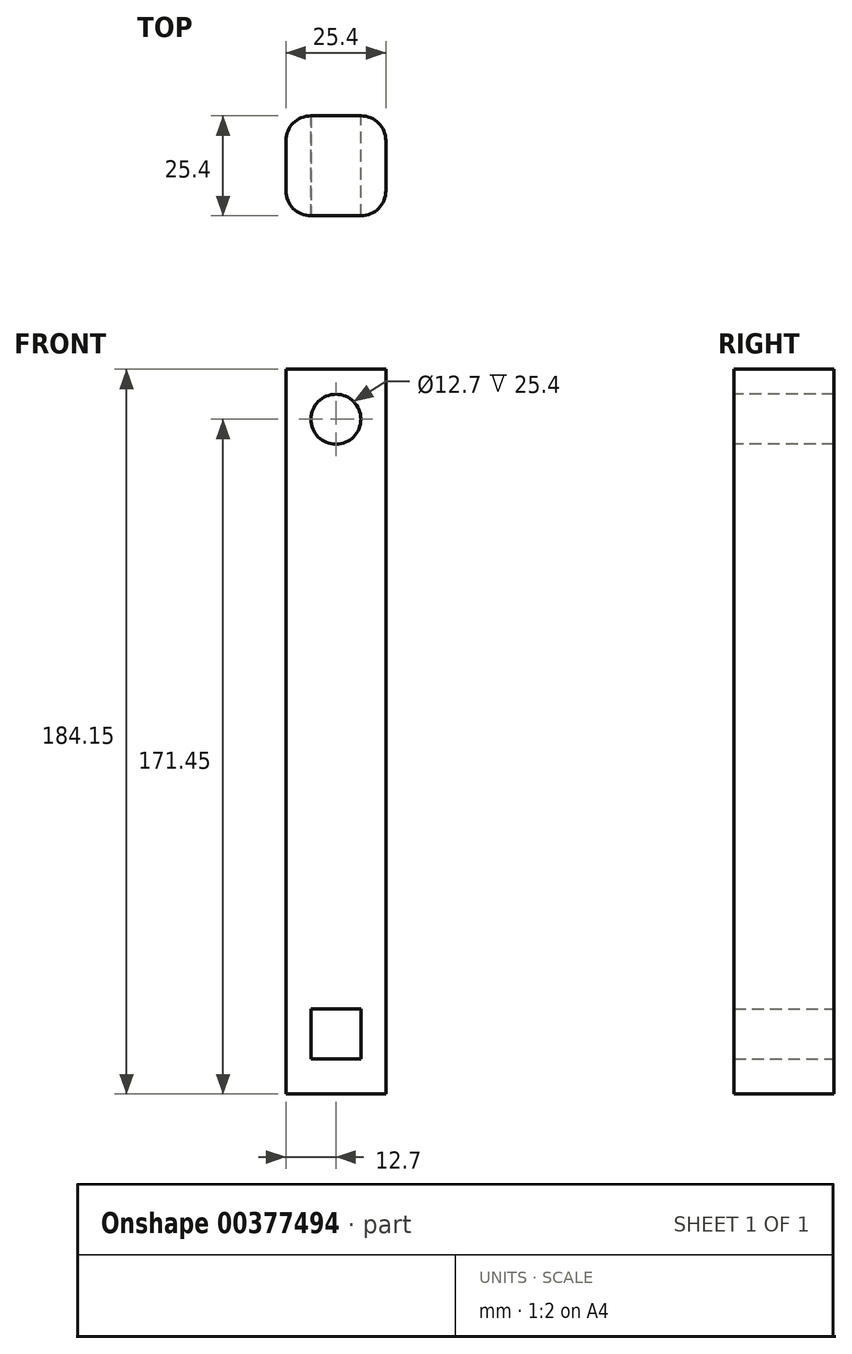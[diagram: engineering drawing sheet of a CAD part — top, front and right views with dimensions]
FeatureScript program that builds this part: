
annotation { "Feature Type Name" : "Feature", "Feature Type Description" : "" }
export const myFeature = defineFeature(function(context is Context, id is Id, definition is map)
    precondition{}
    {
        {
            var Q0;
            Q0=qCreatedBy(makeId("Front.planeOp"),FACE);
            var sketch = newSketch(context, id + "F0", { "sketchPlane" : qUnion([Q0])});
            skLineSegment(sketch, "E0", {"start": v(0, -32) * mm, "end": v(-12.7, -32) * mm});
            skLineSegment(sketch, "E1", {"start": v(-12.7, -32) * mm, "end": v(-12.7, 69.6) * mm});
            skLineSegment(sketch, "E2.MirrorCS", {"start": v(0, -32) * mm, "end": v(12.7, -32) * mm});
            skLineSegment(sketch, "E3.MirrorCS", {"start": v(12.7, -32) * mm, "end": v(12.7, 69.6) * mm});
            skLineSegment(sketch, "E4", {"start": v(12.7, 69.6) * mm, "end": v(-12.7, 69.6) * mm});
            skSolve(sketch);
        }
        {
            var Q0;
            Q0=qSketchRegion(id+"F0",true);
            extrude(context, id + "F1", {"entities" : qUnion([Q0]), "depth" : 25.4 * mm});
        }
        {
            var Q0;
            Q0=makeQuery(id+"F1.opExtrude","CAP_FACE",FACE,{"disambiguationData":[OSD([sQuery(id+"F0.wireOp",EDGE,"E0"),sQuery(id+"F0.wireOp",EDGE,"E1"),sQuery(id+"F0.wireOp",EDGE,"E2.MirrorCS"),sQuery(id+"F0.wireOp",EDGE,"E3.MirrorCS"),sQuery(id+"F0.wireOp",EDGE,"E4")])],"isStart":false});
            var sketch = newSketch(context, id + "F2", { "sketchPlane" : qUnion([Q0])});
            skLineSegment(sketch, "E5", {"start": v(0, 69.6) * mm, "end": v(0, -32) * mm});
            skLineSegment(sketch, "E6", {"start": v(0, -32) * mm, "end": v(0, 18.8) * mm});
            skLineSegment(sketch, "E7", {"start": v(0, 18.8) * mm, "end": v(0, -6.6) * mm});
            skLineSegment(sketch, "E8", {"start": v(0, -6.6) * mm, "end": v(0, 18.8) * mm});
            skLineSegment(sketch, "E9", {"start": v(0, 18.8) * mm, "end": v(0, 69.6) * mm});
            skLineSegment(sketch, "E10", {"start": v(0, 69.6) * mm, "end": v(0, 44.2) * mm});
            skLineSegment(sketch, "E11", {"start": v(0, 69.6) * mm, "end": v(0, 56.9) * mm});
            skLineSegment(sketch, "E12", {"start": v(0, -32) * mm, "end": v(0, -6.6) * mm});
            skLineSegment(sketch, "E13", {"start": v(0, -6.6) * mm, "end": v(0, -19.3) * mm});
            skSolve(sketch);
        }
        {
            var Q0;
            Q0=sQuery(id+"F2.wireOp",VERTEX,"E11.end");
            var Q1;
            Q1=makeQuery(id+"F1.opExtrude","SWEPT_BODY",BODY,{"disambiguationData":[OSD([sQuery(id+"F0.wireOp",EDGE,"E0"),sQuery(id+"F0.wireOp",EDGE,"E1"),sQuery(id+"F0.wireOp",EDGE,"E2.MirrorCS"),sQuery(id+"F0.wireOp",EDGE,"E3.MirrorCS"),sQuery(id+"F0.wireOp",EDGE,"E4")])]});
            hole(context, id + "F3", {"style" : HoleStyle.SIMPLE, "endStyle" : HoleEndStyle.BLIND, "holeDiameter" : 12.7 * mm, "holeDepth" : 254 * mm, "tappedDepth" : 12.7 * mm, "tapClearance" : 3, "locations" : qUnion([Q0]), "scope" : qUnion([Q1])});
        }
        {
            var Q0;
            Q0=makeQuery(id+"F1.opExtrude","CAP_FACE",FACE,{"disambiguationData":[OSD([sQuery(id+"F0.wireOp",EDGE,"E0"),sQuery(id+"F0.wireOp",EDGE,"E1"),sQuery(id+"F0.wireOp",EDGE,"E2.MirrorCS"),sQuery(id+"F0.wireOp",EDGE,"E3.MirrorCS"),sQuery(id+"F0.wireOp",EDGE,"E4")])],"isStart":false});
            var sketch = newSketch(context, id + "F4", { "sketchPlane" : qUnion([Q0])});
            skLineSegment(sketch, "E14", {"start": v(12.7, -32) * mm, "end": v(12.7, -114.56) * mm});
            skLineSegment(sketch, "E15", {"start": v(-12.7, -32) * mm, "end": v(-12.7, -114.56) * mm});
            skLineSegment(sketch, "E16", {"start": v(12.7, -114.56) * mm, "end": v(-12.7, -114.56) * mm});
            skSolve(sketch);
        }
        {
            var Q0;
            Q0=makeQuery(id+"F4.imprint","IMPRINT",FACE,{"disambiguationData":[TD([[makeQuery(id+"F4.imprint","IMPRINT",EDGE,{"derivedFrom":sQuery(id+"F4.wireOp",EDGE,"E14")}),-1.0]])]});
            extrude(context, id + "F5", {"entities" : qUnion([Q0]), "operationType" : NewBodyOperationType.ADD, "depth" : -25.4 * mm});
        }
        {
            var Q0;
            {var subQ0=sQuery(id+"F0.wireOp",EDGE,"E2.MirrorCS");var subQ1=sQuery(id+"F0.wireOp",EDGE,"E0");Q0=makeQuery(id+"F5.boolean.opBoolean","MERGE",FACE,{"derivedFrom":[makeQuery(id+"F1.opExtrude","CAP_FACE",FACE,{"disambiguationData":[OSD([subQ1,sQuery(id+"F0.wireOp",EDGE,"E1"),subQ0,sQuery(id+"F0.wireOp",EDGE,"E3.MirrorCS"),sQuery(id+"F0.wireOp",EDGE,"E4")])],"isStart":true}),makeQuery(id+"F5.opExtrude","CAP_FACE",FACE,{"disambiguationData":[OSD([subQ1,subQ0,sQuery(id+"F4.wireOp",EDGE,"E14"),sQuery(id+"F4.wireOp",EDGE,"E15"),sQuery(id+"F4.wireOp",EDGE,"E16")])],"isStart":false})]});}
            var sketch = newSketch(context, id + "F6", { "sketchPlane" : qUnion([Q0])});
            skLineSegment(sketch, "E17", {"start": v(0, -114.56) * mm, "end": v(0, -99.32) * mm});
            skLineSegment(sketch, "E18.bottom", {"start": v(6.35, -105.67) * mm, "end": v(-6.35, -105.67) * mm});
            skLineSegment(sketch, "E18.top", {"start": v(6.35, -92.97) * mm, "end": v(-6.35, -92.97) * mm});
            skLineSegment(sketch, "E18.left", {"start": v(6.35, -105.67) * mm, "end": v(6.35, -92.97) * mm});
            skLineSegment(sketch, "E18.right", {"start": v(-6.35, -105.67) * mm, "end": v(-6.35, -92.97) * mm});
            skPoint(sketch, "E18.middle", {"position": v(0, -99.32) * mm});
            skSolve(sketch);
        }
        {
            var Q0;
            Q0=qSketchRegion(id+"F6",true);
            extrude(context, id + "F7", {"entities" : qUnion([Q0]), "operationType" : NewBodyOperationType.REMOVE, "oppositeDirection" : true, "depth" : 25.4 * mm});
        }
        {
            var Q0;
            Q0=makeQuery(id+"F5.boolean.opBoolean","MERGE",EDGE,{"derivedFrom":[makeQuery(id+"F1.opExtrude","CAP_EDGE",EDGE,{"disambiguationData":[OSD([sQuery(id+"F0.wireOp",EDGE,"E3.MirrorCS")])],"isStart":true}),makeQuery(id+"F5.opExtrude","CAP_EDGE",EDGE,{"disambiguationData":[OSD([sQuery(id+"F4.wireOp",EDGE,"E14")])],"isStart":false})]});
            var Q1;
            Q1=makeQuery(id+"F5.boolean.opBoolean","MERGE",EDGE,{"derivedFrom":[makeQuery(id+"F1.opExtrude","CAP_EDGE",EDGE,{"disambiguationData":[OSD([sQuery(id+"F0.wireOp",EDGE,"E1")])],"isStart":true}),makeQuery(id+"F5.opExtrude","CAP_EDGE",EDGE,{"disambiguationData":[OSD([sQuery(id+"F4.wireOp",EDGE,"E15")])],"isStart":false})]});
            var Q2;
            Q2=makeQuery(id+"F5.boolean.opBoolean","MERGE",EDGE,{"derivedFrom":[makeQuery(id+"F1.opExtrude","CAP_EDGE",EDGE,{"disambiguationData":[OSD([sQuery(id+"F0.wireOp",EDGE,"E1")])],"isStart":false}),makeQuery(id+"F5.opExtrude","CAP_EDGE",EDGE,{"disambiguationData":[OSD([sQuery(id+"F4.wireOp",EDGE,"E15")])],"isStart":true})]});
            var Q3;
            Q3=makeQuery(id+"F5.boolean.opBoolean","MERGE",EDGE,{"derivedFrom":[makeQuery(id+"F1.opExtrude","CAP_EDGE",EDGE,{"disambiguationData":[OSD([sQuery(id+"F0.wireOp",EDGE,"E3.MirrorCS")])],"isStart":false}),makeQuery(id+"F5.opExtrude","CAP_EDGE",EDGE,{"disambiguationData":[OSD([sQuery(id+"F4.wireOp",EDGE,"E14")])],"isStart":true})]});
            fillet(context, id + "F8", {"entities" : qUnion([Q0, Q1, Q2, Q3]), "radius" : 6.35 * mm, "tangentPropagation" : true, "allowEdgeOverflow" : false});
        }
    });
